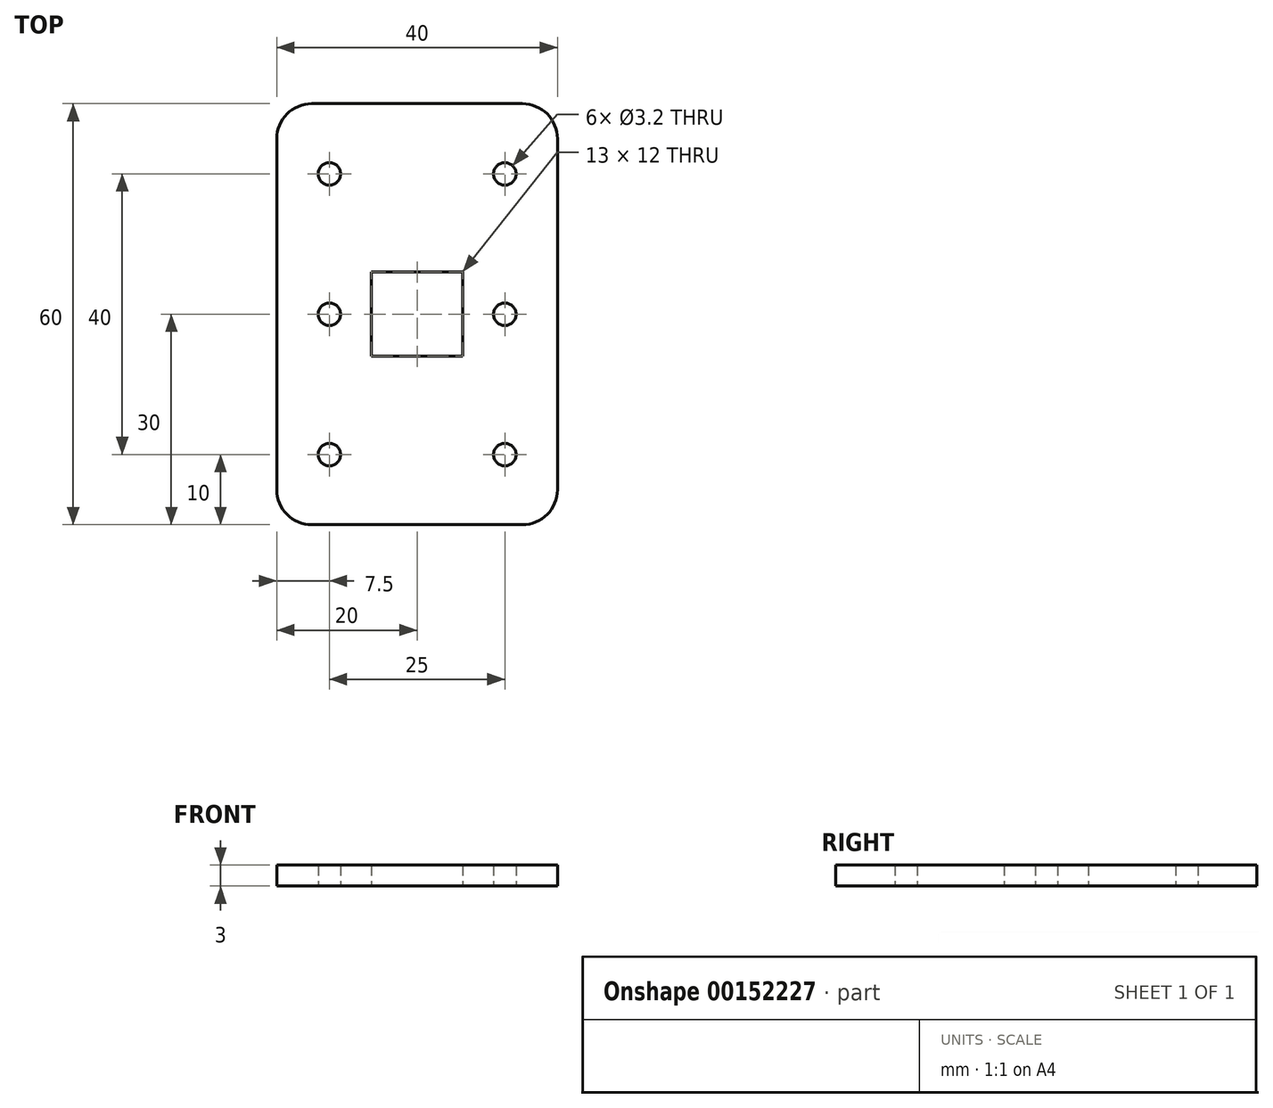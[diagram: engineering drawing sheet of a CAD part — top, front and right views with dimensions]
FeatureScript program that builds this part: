
annotation { "Feature Type Name" : "Feature", "Feature Type Description" : "" }
export const myFeature = defineFeature(function(context is Context, id is Id, definition is map)
    precondition{}
    {
        {
            var Q0;
            Q0=qCreatedBy(makeId("Top.planeOp"),FACE);
            var sketch = newSketch(context, id + "F0", { "sketchPlane" : qUnion([Q0])});
            skLineSegment(sketch, "E0.bottom", {"start": v(20, 30) * mm, "end": v(-20, 30) * mm});
            skLineSegment(sketch, "E0.top", {"start": v(20, -30) * mm, "end": v(-20, -30) * mm});
            skLineSegment(sketch, "E0.left", {"start": v(20, 30) * mm, "end": v(20, -30) * mm});
            skLineSegment(sketch, "E0.right", {"start": v(-20, 30) * mm, "end": v(-20, -30) * mm});
            skPoint(sketch, "E0.middle", {"position": v(0, 0) * mm});
            skLineSegment(sketch, "E1", {"start": v(0, 0) * mm, "end": v(12.5, 0) * mm});
            skLineSegment(sketch, "E2", {"start": v(0, 0) * mm, "end": v(-12.5, 0) * mm});
            skLineSegment(sketch, "E3", {"start": v(-12.5, 0) * mm, "end": v(-12.5, 20) * mm});
            skLineSegment(sketch, "E4", {"start": v(12.5, 0) * mm, "end": v(12.5, 20) * mm});
            skLineSegment(sketch, "E5", {"start": v(12.5, 0) * mm, "end": v(12.5, -20) * mm});
            skLineSegment(sketch, "E6", {"start": v(-12.5, 0) * mm, "end": v(-12.5, -20) * mm});
            skCircle(sketch, "E7", {"center": v(-12.5, -20) * mm, "radius": 1.6 * mm});
            skCircle(sketch, "E8", {"center": v(-12.5, 20) * mm, "radius": 1.6 * mm});
            skCircle(sketch, "E9", {"center": v(-12.5, 0) * mm, "radius": 1.6 * mm});
            skCircle(sketch, "E10", {"center": v(12.5, 0) * mm, "radius": 1.6 * mm});
            skCircle(sketch, "E11", {"center": v(12.5, 20) * mm, "radius": 1.6 * mm});
            skCircle(sketch, "E12", {"center": v(12.5, -20) * mm, "radius": 1.6 * mm});
            skLineSegment(sketch, "E13.bottom", {"start": v(6.5, 6) * mm, "end": v(-6.5, 6) * mm});
            skLineSegment(sketch, "E13.top", {"start": v(6.5, -6) * mm, "end": v(-6.5, -6) * mm});
            skLineSegment(sketch, "E13.left", {"start": v(6.5, 6) * mm, "end": v(6.5, -6) * mm});
            skLineSegment(sketch, "E13.right", {"start": v(-6.5, 6) * mm, "end": v(-6.5, -6) * mm});
            skSolve(sketch);
        }
        {
            var Q0;
            Q0 = qSketchRegion(id + "F0", true);
            extrude(context, id + "F1", {"entities" : qUnion([Q0]), "depth" : 3 * mm, "offsetDistance" : 25 * mm});
        }
        {
            var Q0;
            Q0=makeQuery(id+"F1.opExtrude","SWEPT_EDGE",EDGE,{"disambiguationData":[OSD([sQuery(id+"F0.wireOp",EDGE,"E0.top"),sQuery(id+"F0.wireOp",EDGE,"E0.left")])]});
            var Q1;
            Q1=makeQuery(id+"F1.opExtrude","SWEPT_EDGE",EDGE,{"disambiguationData":[OSD([sQuery(id+"F0.wireOp",EDGE,"E0.bottom"),sQuery(id+"F0.wireOp",EDGE,"E0.left")])]});
            var Q2;
            Q2=makeQuery(id+"F1.opExtrude","SWEPT_EDGE",EDGE,{"disambiguationData":[OSD([sQuery(id+"F0.wireOp",EDGE,"E0.top"),sQuery(id+"F0.wireOp",EDGE,"E0.right")])]});
            var Q3;
            Q3=makeQuery(id+"F1.opExtrude","SWEPT_EDGE",EDGE,{"disambiguationData":[OSD([sQuery(id+"F0.wireOp",EDGE,"E0.bottom"),sQuery(id+"F0.wireOp",EDGE,"E0.right")])]});
            fillet(context, id + "F2", {"entities" : qUnion([Q0, Q1, Q2, Q3]), "radius" : 5 * mm, "tangentPropagation" : true, "allowEdgeOverflow" : false});
        }
    });
